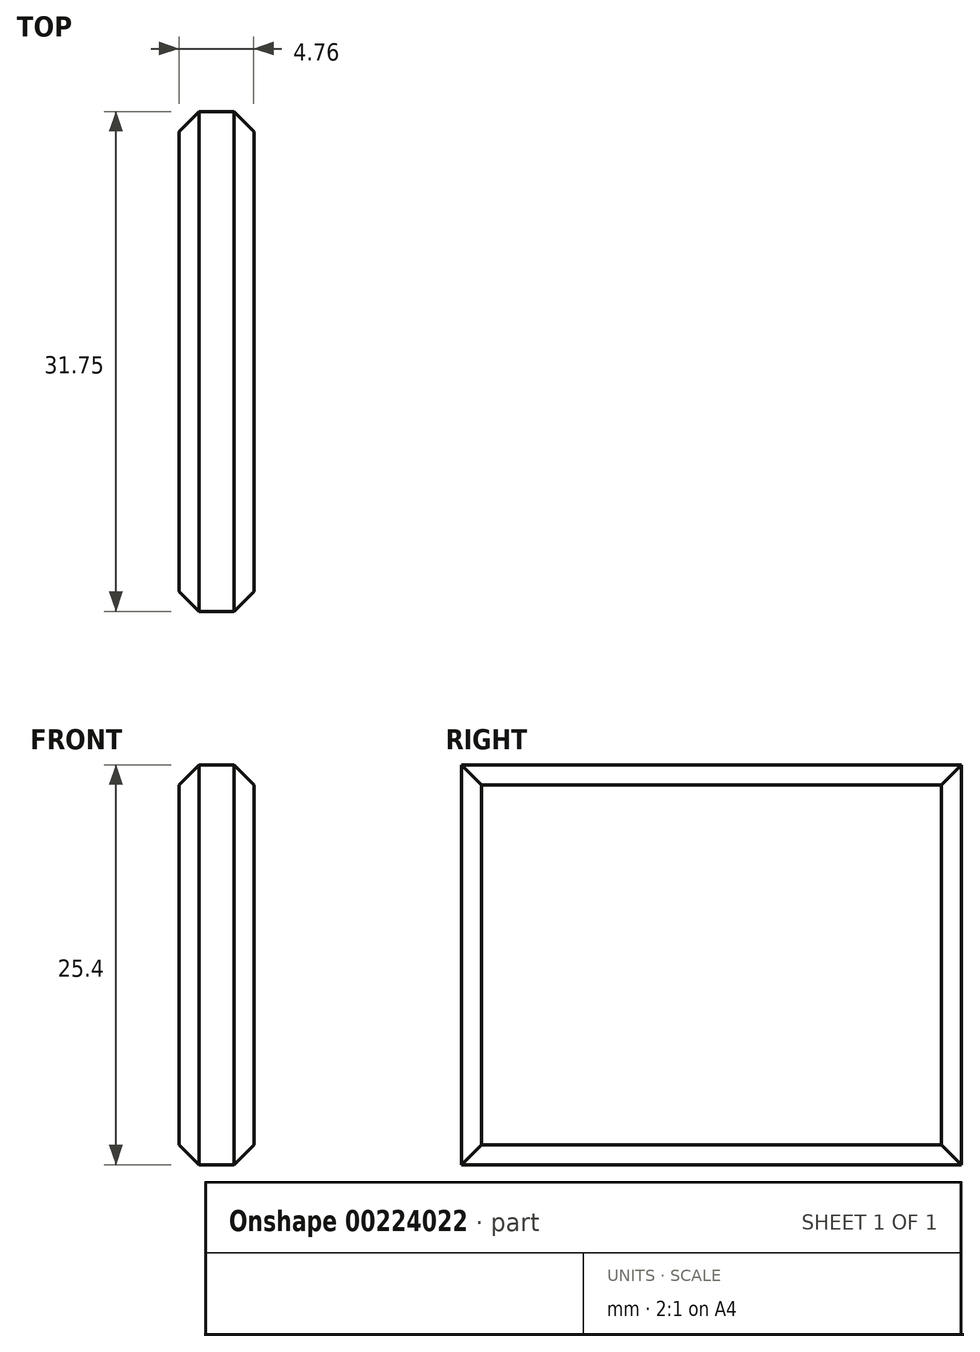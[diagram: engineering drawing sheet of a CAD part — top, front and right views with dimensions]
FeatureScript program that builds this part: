
annotation { "Feature Type Name" : "Feature", "Feature Type Description" : "" }
export const myFeature = defineFeature(function(context is Context, id is Id, definition is map)
    precondition{}
    {
        {
            var Q0;
            Q0=qCreatedBy(makeId("Front.planeOp"),FACE);
            var sketch = newSketch(context, id + "F0", { "sketchPlane" : qUnion([Q0])});
            skLineSegment(sketch, "E0.bottom", {"start": v(2.38, 12.7) * mm, "end": v(-2.38, 12.7) * mm});
            skLineSegment(sketch, "E0.top", {"start": v(2.38, -12.7) * mm, "end": v(-2.38, -12.7) * mm});
            skLineSegment(sketch, "E0.left", {"start": v(2.38, 12.7) * mm, "end": v(2.38, -12.7) * mm});
            skLineSegment(sketch, "E0.right", {"start": v(-2.38, 12.7) * mm, "end": v(-2.38, -12.7) * mm});
            skPoint(sketch, "E0.middle", {"position": v(0, 0) * mm});
            skSolve(sketch);
        }
        {
            var Q0;
            Q0 = qSketchRegion(id + "F0", true);
            extrude(context, id + "F1", {"entities" : qUnion([Q0]), "depth" : 31.75 * mm});
        }
        {
            var Q0;
            Q0=makeQuery(id+"F1.opExtrude","SWEPT_FACE",FACE,{"disambiguationData":[OSD([sQuery(id+"F0.wireOp",EDGE,"E0.left")])]});
            var Q1;
            Q1=makeQuery(id+"F1.opExtrude","SWEPT_FACE",FACE,{"disambiguationData":[OSD([sQuery(id+"F0.wireOp",EDGE,"E0.right")])]});
            chamfer(context, id + "F2", {"entities" : qUnion([Q0, Q1]), "width" : 1.27 * mm, "tangentPropagation" : true});
        }
    });
